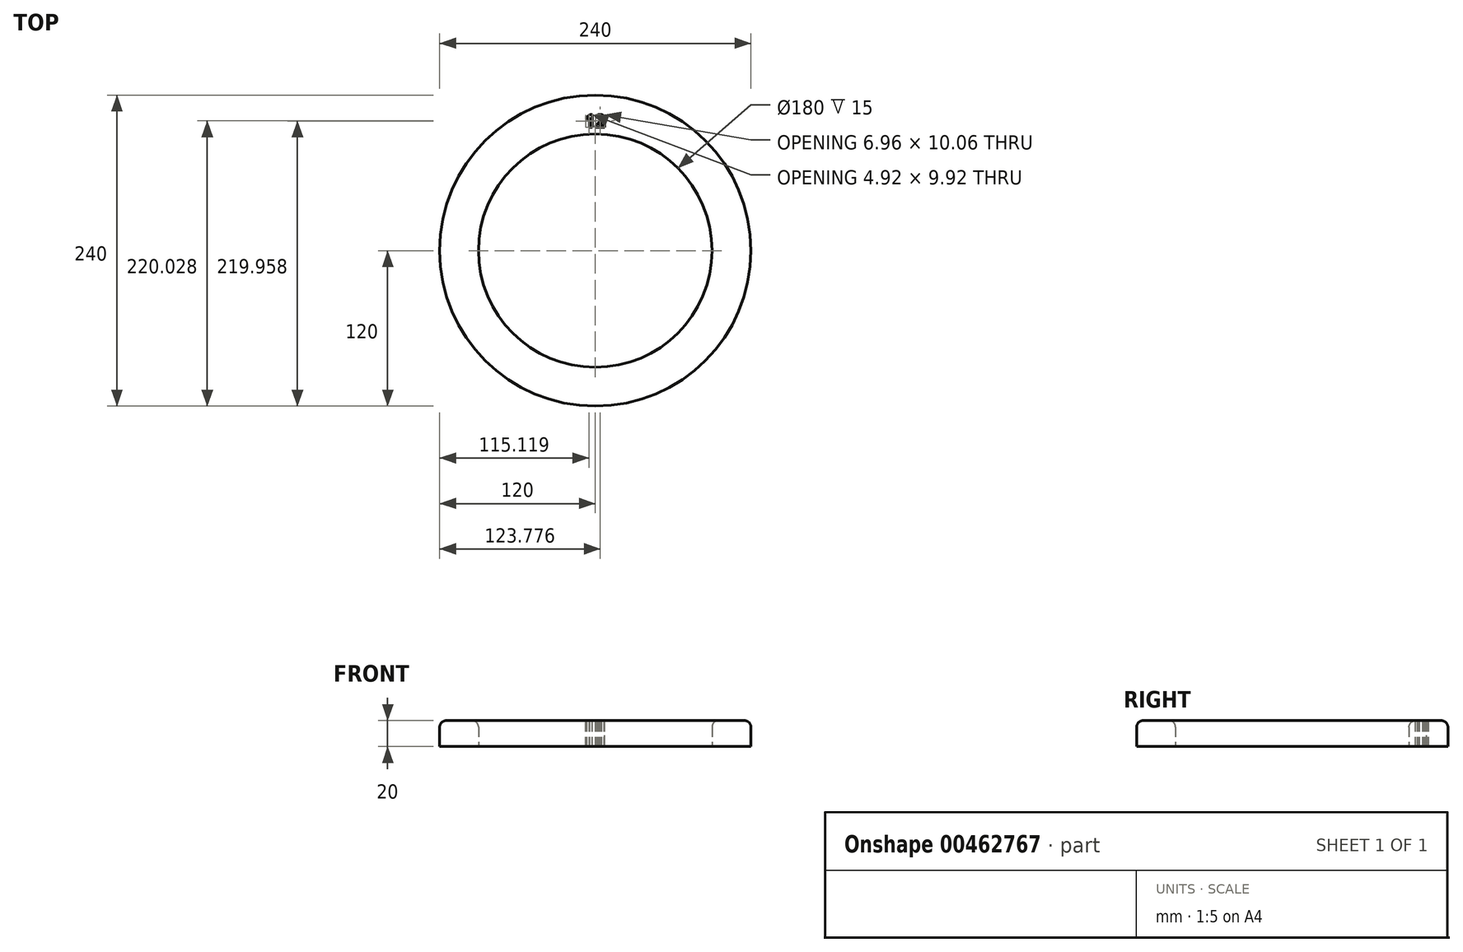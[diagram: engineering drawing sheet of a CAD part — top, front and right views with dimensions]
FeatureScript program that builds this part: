
annotation { "Feature Type Name" : "Feature", "Feature Type Description" : "" }
export const myFeature = defineFeature(function(context is Context, id is Id, definition is map)
    precondition{}
    {
        {
            var Q0;
            Q0=qCreatedBy(makeId("Top.planeOp"),FACE);
            var sketch = newSketch(context, id + "F0", { "sketchPlane" : qUnion([Q0])});
            skCircle(sketch, "E0", {"center": v(0, 0) * mm, "radius": 120 * mm});
            skCircle(sketch, "E1", {"center": v(0, 0) * mm, "radius": 90 * mm});
            skSolve(sketch);
        }
        {
            var Q0;
            Q0 = qSketchRegion(id + "F0", true);
            extrude(context, id + "F1", {"entities" : qUnion([Q0]), "depth" : 20 * mm});
        }
        {
            var Q0;
            Q0=makeQuery(id+"F1.opExtrude","CAP_FACE",FACE,{"disambiguationData":[OSD([sQuery(id+"F0.wireOp",EDGE,"E0"),sQuery(id+"F0.wireOp",EDGE,"E1")])],"isStart":false});
            var sketch = newSketch(context, id + "F2", { "sketchPlane" : qUnion([Q0])});
            skText(sketch, "E2", { "text": "12", "fontName": "OpenSans-Bold.ttf"});
            skLineSegment(sketch, "E3", {"start": v(0, 92.68) * mm, "end": v(0, -90.1) * mm, "construction": true});
            skLineSegment(sketch, "E4", {"start": v(93.53, 0) * mm, "end": v(-89.46, 0) * mm, "construction": true});
            const initialGuessF2  = {"E2": [-0.00816, 0.095, 1, 0, 0.01]};
            skSetInitialGuess(sketch, initialGuessF2);
            skSolve(sketch);
        }
        {
            var Q0;
            Q0 = qSketchRegion(id + "F2", true);
            extrude(context, id + "F3", {"entities" : qUnion([Q0]), "operationType" : NewBodyOperationType.REMOVE, "oppositeDirection" : true, "depth" : 25 * mm});
        }
        {
            var Q0;
            Q0=makeQuery(id+"F1.opExtrude","CAP_EDGE",EDGE,{"disambiguationData":[OSD([sQuery(id+"F0.wireOp",EDGE,"E1")])],"isStart":false});
            var Q1;
            Q1=makeQuery(id+"F1.opExtrude","CAP_EDGE",EDGE,{"disambiguationData":[OSD([sQuery(id+"F0.wireOp",EDGE,"E0")])],"isStart":false});
            fillet(context, id + "F4", {"entities" : qUnion([Q0, Q1]), "radius" : 5 * mm, "tangentPropagation" : true, "allowEdgeOverflow" : false});
        }
    });
